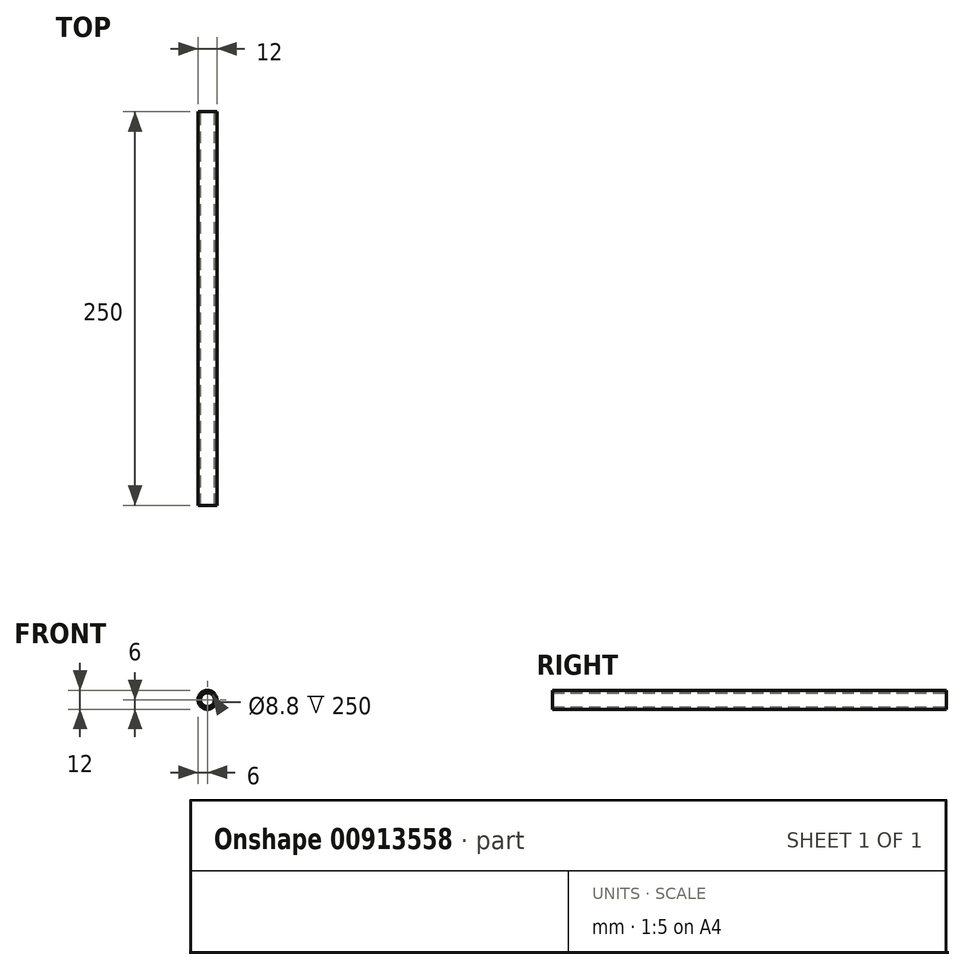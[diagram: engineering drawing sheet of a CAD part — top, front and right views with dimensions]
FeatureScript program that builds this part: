
annotation { "Feature Type Name" : "Feature", "Feature Type Description" : "" }
export const myFeature = defineFeature(function(context is Context, id is Id, definition is map)
    precondition{}
    {
        {
            var Q0;
            Q0=qCreatedBy(makeId("Front.planeOp"),FACE);
            var sketch = newSketch(context, id + "F0", { "sketchPlane" : qUnion([Q0])});
            skCircle(sketch, "E0", {"center": v(0, 0) * mm, "radius": 6 * mm});
            skCircle(sketch, "E1.0", {"center": v(0, 0) * mm, "radius": 4.4 * mm});
            skSolve(sketch);
        }
        {
            var Q0;
            Q0=makeQuery(id+"F0.imprint","IMPRINT",FACE,{"disambiguationData":[TD([[makeQuery(id+"F0.imprint","IMPRINT",EDGE,{"derivedFrom":sQuery(id+"F0.wireOp",EDGE,"E0")}),1.0]])]});
            extrude(context, id + "F1", {"entities" : qUnion([Q0]), "endBound" : BoundingType.SYMMETRIC, "depth" : 250 * mm, "offsetDistance" : 25 * mm});
        }
    });
